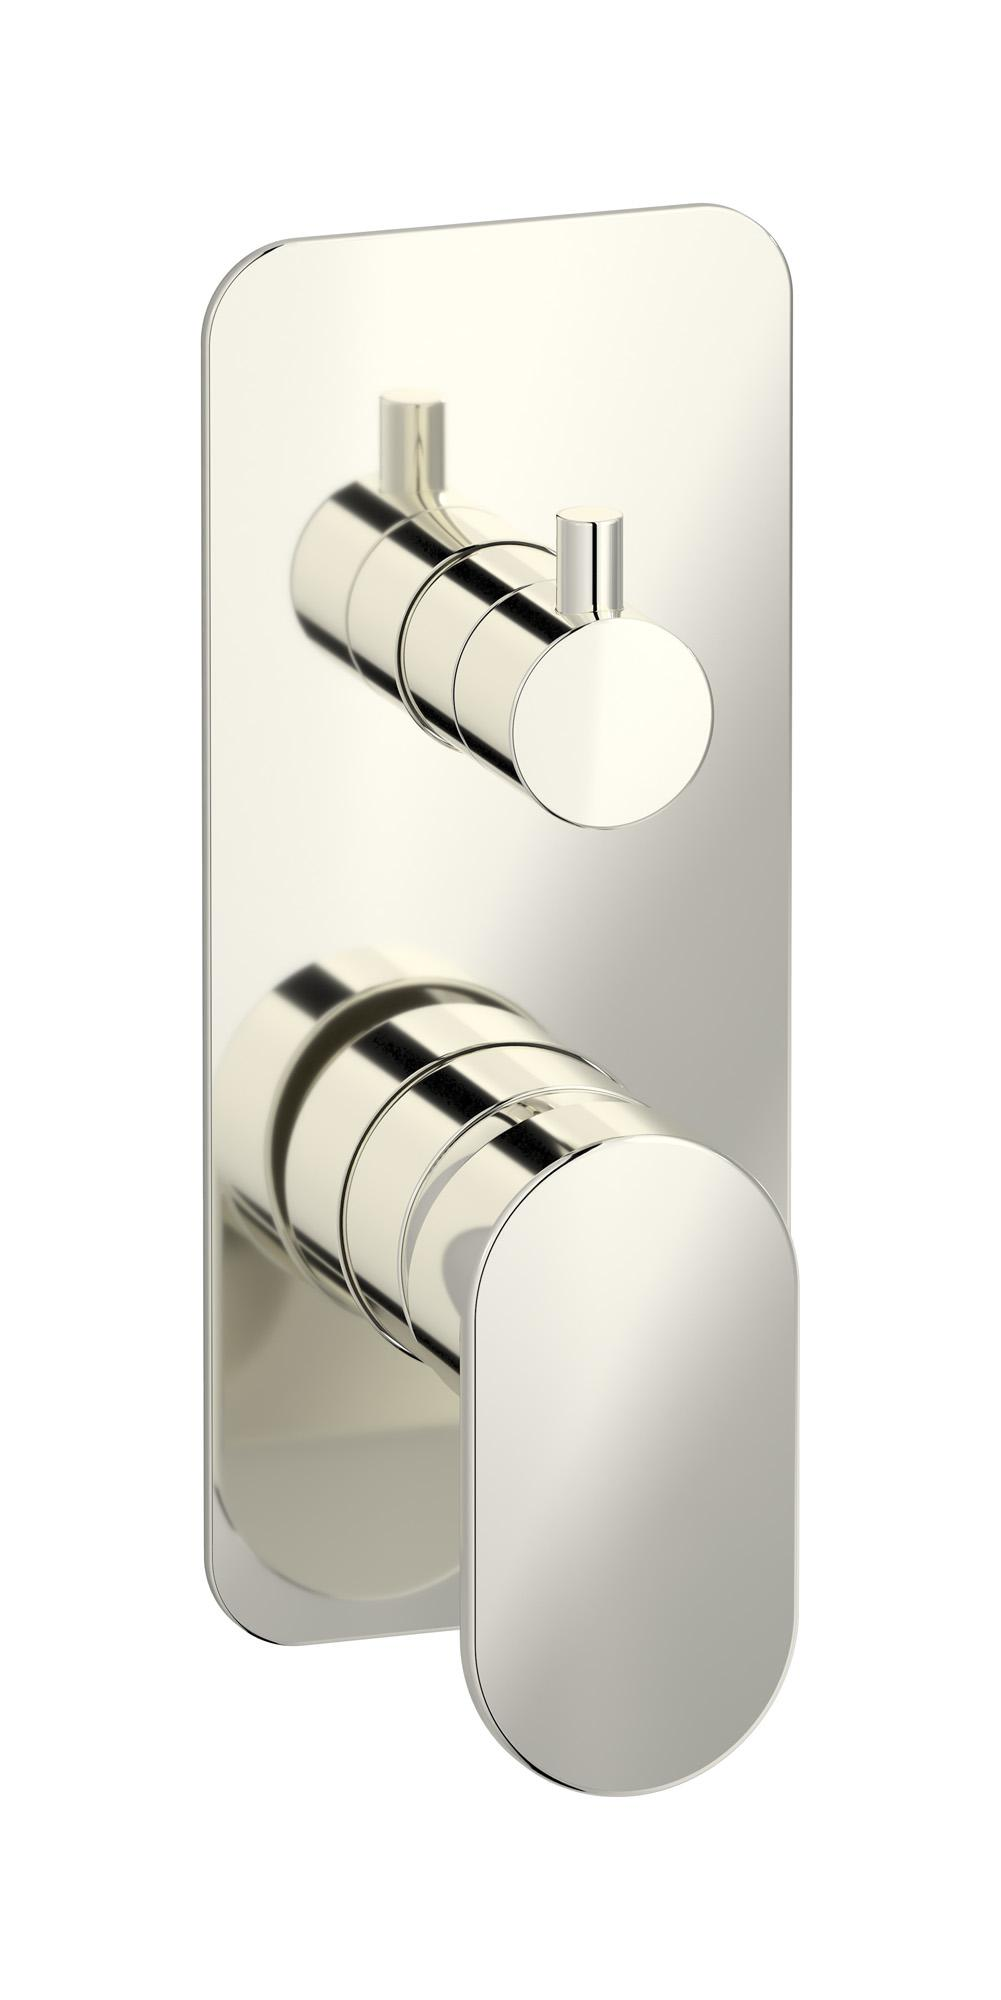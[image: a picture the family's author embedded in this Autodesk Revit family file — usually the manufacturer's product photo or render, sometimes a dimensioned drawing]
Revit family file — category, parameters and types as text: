
# Revit family: K2312
name_source: partatom
category: Apparecchi idraulici
units: mm (PartAtom-declared; Revit-internal decimal feet)

## family parameters
Basato su piano di lavoro = No
Condiviso = No
Mantieni orientamento annotazione = No
Numero OmniClass = 23.45.55.17
Punto di calcolo locali = No
Quota connettore circolare = Usa diametro
Sempre verticale = Sì
Taglio con vuoti quando caricato = No
Tipo di parte = Normale
Titolo OmniClass = Mixing Faucets

## types (9) — shared parameters
Cold water inlet = 10 mm  [stored 0.0328084 ft]
Commenti sul tipo = Wall mixer
Connessione CW = No
Connessione HW = No
Connessione di scarico = No
Connessione di ventilazione = No
Descrizione = Exposed parts for manual wall mixer with three ways diverter
Hot water inlet = 10 mm  [stored 0.0328084 ft]
Produttore = IB Rubinetterie S.p.A.
URL = https://www.weareib.it
zero-valued in all types: Prospetto di default

## per-type parameters (varying)
| type | Finishes surface | Immagine tipo | Modello |
| Chrome | IB_Chrome | K2312CC.jpg | K2312CC |
| Brushed nickel | IB_Brushed nickel | K2312SS.jpg | K2312SS |
| Matt black | IB_matt black | K2312NP.jpg | K2312NP |
| Matt white | IB_matt white | K2312BO.jpg | K2312BO |
| Platinum | IB_Platinum | K2312PL.jpg | K2312PL |
| Pale gold | IB_Pale gold | K2312II.jpg | K2312II |
| Brushed pale gold | IB_brushed pale gold | K2312IS.jpg | K2312IS |
| Rose gold | IB_Rose gold | K2312RS.jpg | K2312RS |
| Gold | IB_gold | K2312OO.jpg | K2312OO |

note: [stored X ft] marks values corroborated as IEEE doubles in the binary element streams (Revit-internal decimal feet)
